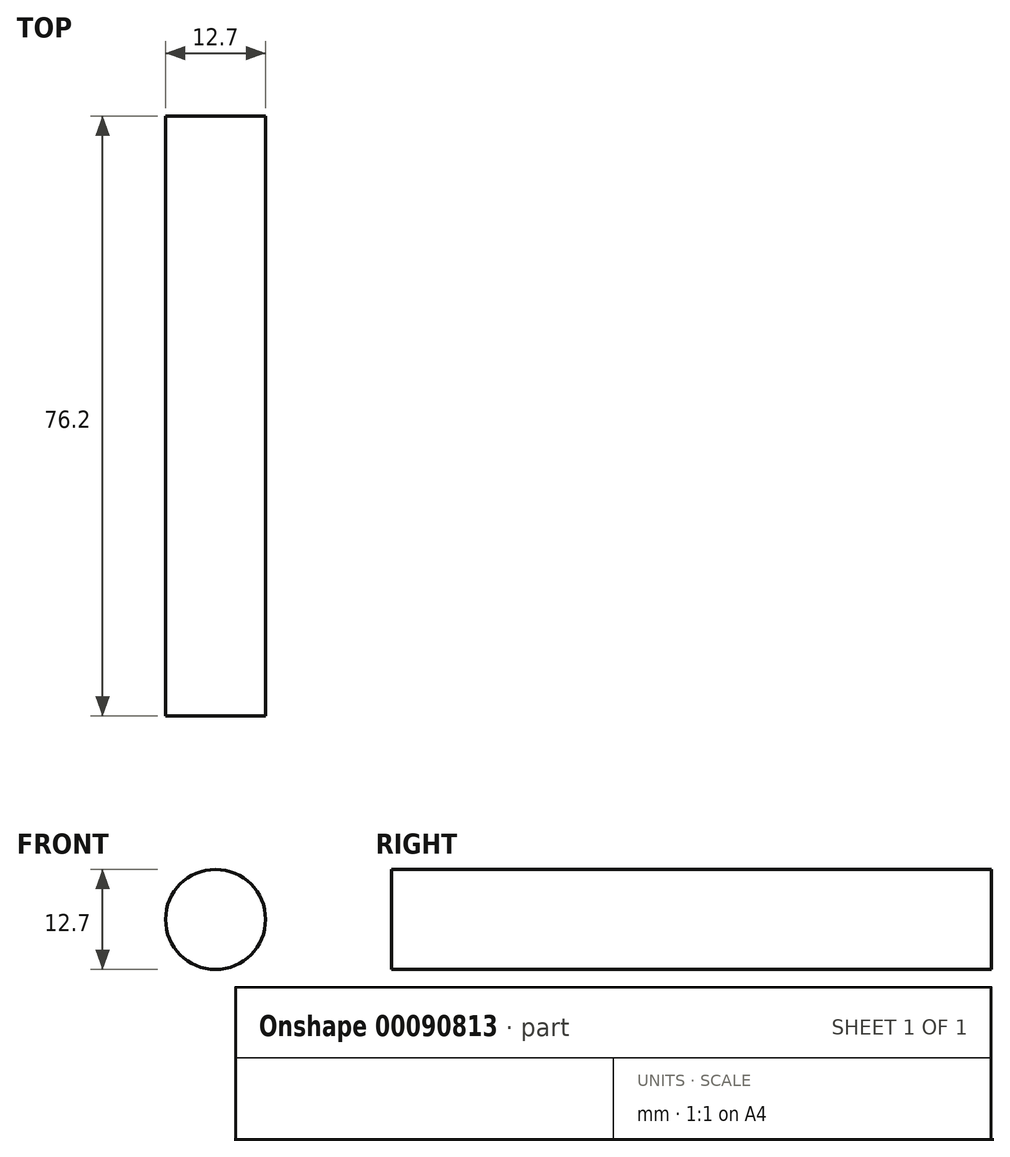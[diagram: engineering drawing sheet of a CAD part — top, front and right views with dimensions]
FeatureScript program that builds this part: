
annotation { "Feature Type Name" : "Feature", "Feature Type Description" : "" }
export const myFeature = defineFeature(function(context is Context, id is Id, definition is map)
    precondition{}
    {
        {
            var Q0;
            Q0=qCreatedBy(makeId("Front.planeOp"),FACE);
            var sketch = newSketch(context, id + "F0", { "sketchPlane" : qUnion([Q0])});
            skCircle(sketch, "E0", {"center": v(0, 0) * mm, "radius": 6.35 * mm});
            skSolve(sketch);
        }
        {
            var Q0;
            Q0 = qSketchRegion(id + "F0", true);
            extrude(context, id + "F1", {"entities" : qUnion([Q0]), "depth" : 76.2 * mm});
        }
    });
